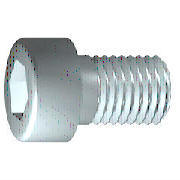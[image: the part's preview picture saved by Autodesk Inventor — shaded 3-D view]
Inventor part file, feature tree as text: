
AUTODESK INVENTOR PART (.ipt)
format: ipt  version: 2018 (Build 220112000, 112)  size: 184,320 bytes
history: native  units: mm (DEFAULTED — no unit token found)
features: sketch x2, extrude x1, plane x1, fillet x1
ambient origin geometry x7: Origin, YZ Plane, XY Plane, X Axis, Y Axis, Z Axis, Center Point
bodies: Solid1 (feature_tree), Body (feature_tree)
feature tree (5):
  extrude  "Slot"  Depth=5.0mm
  plane  "Work Plane1"
  fillet  "Fillet2"  Radius=5.0mm
  sketch  "Sketch1"  dims[d1=22.0mm d2=0.49086mm d3=5.0mm]
  sketch  "Sketch2"  dims[d4=2.5mm d5=60.0deg d6=5.0mm d7=5.0mm d8=4.618802mm d9=8.5mm d10=90.0deg d11=10.0mm d12=0.0mm d13=22.0mm d14=0.0mm d15=0.49076mm d16=0.49076mm d17=0.5mm d19=0.0mm d26=40.0mm d27=45.0deg d28=0.0mm d29=0.0mm d30=0.1mm]
